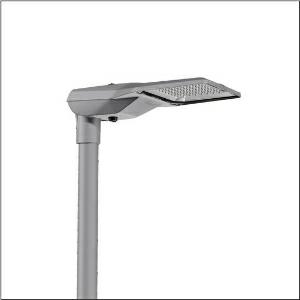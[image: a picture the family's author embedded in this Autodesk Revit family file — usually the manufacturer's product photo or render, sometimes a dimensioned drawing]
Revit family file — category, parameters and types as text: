
# Revit family: streetlight_sl_21_midi___p0_5a_5xe3v33t08mb_d4c3
name_source: partatom
category: Lighting Fixtures
units: mm (PartAtom-declared; Revit-internal decimal feet)

## family parameters
Cut with Voids When Loaded = No
Host = Face
Light Source = No
Part Type = Normal
Room Calculation Point = No
Round Connector Dimension = Use Diameter
Shared = No

## types (1)
- --- (1 x LED, 17960 lm, 136 W, 3000K)
    Apparent Load = 136 VA
    CIE Flux Codes = 37 73 96 100 100
    Color Rendering = 70
    Color Temperature = 3000K
    Default Elevation = 1800 mm
    Description = Streetlight SL 21 midi, mast luminaire, primary light control with lens, of PMMA, primary optical cover: cover, of toughened safety glass, transparent, light distribution: P0.5a, light emission: direct distribution, primary light characteristic: asymmetric, installation type: post-top, side-entry, LED, High Power LED, rated luminous flux: 17.960lm, luminous efficacy: 132lm/W, light colour: 730, colour temperature: 3000K, control gear: D4i, control: pre-setting: logarithmic dimming characteristic, flexible luminous flux parameterisation, time-dependent luminous flux control, constant luminous flux control, overheat protection, mains connection: 230..240V, AC, 50/60Hz, start of lifetime: 136W, end of service life: 142W, reduction: 61W, luminaire housing, of diecast aluminium, powder-coated, SITECO metallic grey (DB 702S), corrosivity category C5 high according to DIN EN ISO 12944, multi-level sealing system, sealing non-destructively replaceable, inclination adjustable: 0°, 5°, 10°, 15°, please order mast flange separately, length: 644mm, width: 335mm, height: 110mm, mast flange for spigot size: 42mm (side-entry): 5XC10008XM4, 60/48mm (side-entry/post-top): 5XC10108XM2, 76/60mm (side-entry/post-top): 5XC10108XM1, mounting height: 4..8m, Smart Interface below and above, protection rating (complete): IP66, insulation class (complete): insulation class II (safety insulation), certification: CE, ENEC, ENEC+, VDE, impact resistance: IK10, permissible operating ambient temperature for outdoor applications: -40..+50°C, standard-compliant lighting for roads and squares, packaging unit: 1 piece

Light Distribution: P0.5a
    Height = 111 mm
    Lamp = 1 x LED
    Lamp Light Flux = 17960 lm
    Lamp Power = 136 W
    Lamp count = 1
    Length = 644 mm
    Luminous efficacy = 132 lm/W
    Manufacturer = Siteco
    ModVariant = No
    Model = 5XE3V33T08MB
    Number of Poles = 1
    OnlyDefault = Yes
    Power Factor = 1
    Product Name = Streetlight SL 21 midi | P0.5a
    Product group = mast luminaire | pylon top
    ProductGroupID = 6100
    Protection Class = Protection class II
    Protection Degree = IP 66
    RLX_Detail_Level = 1
    RLX_Emergency_Light_Flux = 0 lm
    RLX_Emergency_Type = 0
    RLX_Emergency_Type_DB = No
    RlxData = <blob elided: 90313 chars, md5=3851777a>
    Socket = socket
    Standby Power = 0 W
    System Light Flux = 17960 lm
    System Power = 136 W
    Type Comments = factory setting: luminous flux: 100 % | dim-lin: 254 | 695 mA
    Type Image = l_1004304.jpg
    URL = http://relux.com
    VarID = @adj_077617
    Voltage = 0 V
    Weight = 0.00 kg
    Width = 336 mm

## geometry (parser evidence)
native form markers: Blend x4, Sweep x9
no freeform markers — native parametric forms only
